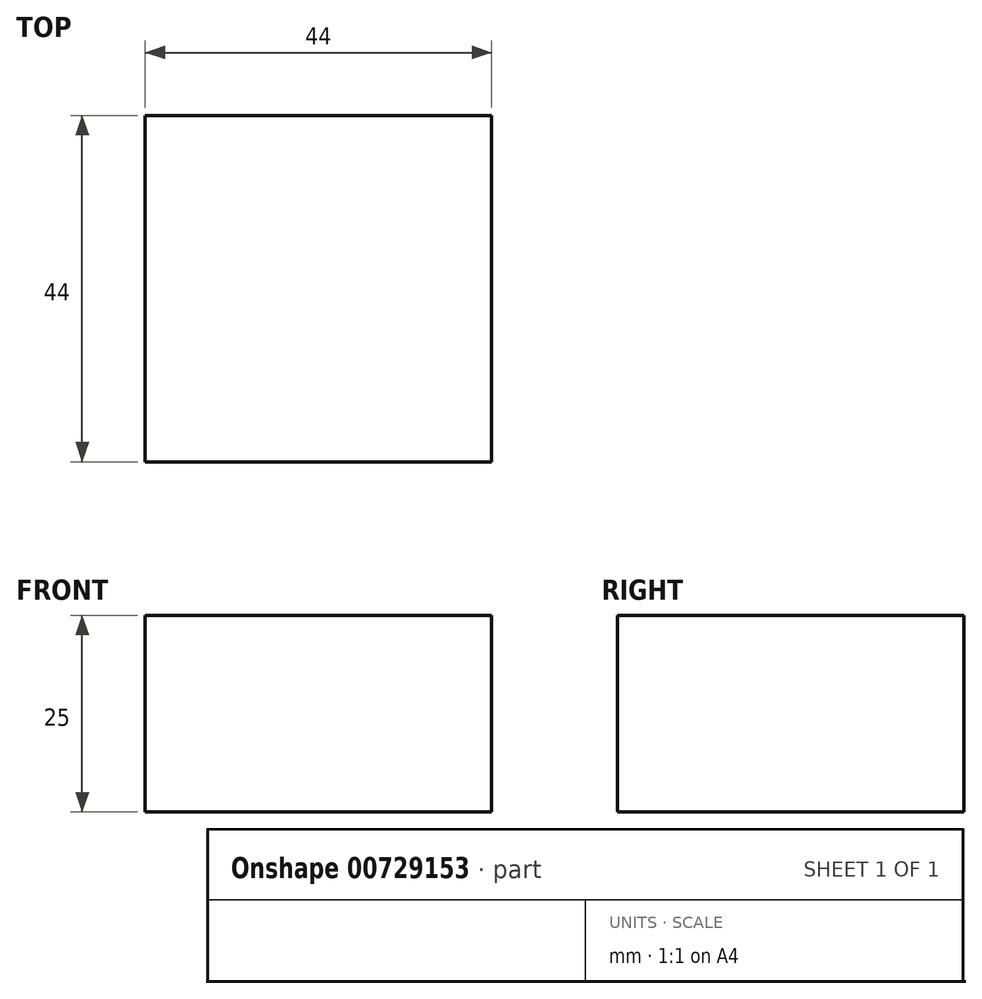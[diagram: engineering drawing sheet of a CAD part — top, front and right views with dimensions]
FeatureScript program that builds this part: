
annotation { "Feature Type Name" : "Feature", "Feature Type Description" : "" }
export const myFeature = defineFeature(function(context is Context, id is Id, definition is map)
    precondition{}
    {
        {
            var Q0;
            Q0=qCreatedBy(makeId("Top.planeOp"),FACE);
            var sketch = newSketch(context, id + "F0", { "sketchPlane" : qUnion([Q0])});
            skLineSegment(sketch, "E0.bottom", {"start": v(22, -22) * mm, "end": v(-22, -22) * mm});
            skLineSegment(sketch, "E0.top", {"start": v(22, 22) * mm, "end": v(-22, 22) * mm});
            skLineSegment(sketch, "E0.left", {"start": v(22, -22) * mm, "end": v(22, 22) * mm});
            skLineSegment(sketch, "E0.right", {"start": v(-22, -22) * mm, "end": v(-22, 22) * mm});
            skPoint(sketch, "E0.middle", {"position": v(0, 0) * mm});
            skSolve(sketch);
        }
        {
            var Q0;
            Q0=makeQuery(id+"F0.imprint","IMPRINT",FACE,{"disambiguationData":[TD([[makeQuery(id+"F0.imprint","IMPRINT",EDGE,{"derivedFrom":sQuery(id+"F0.wireOp",EDGE,"E0.bottom")}),-1.0]])]});
            extrude(context, id + "F1", {"entities" : qUnion([Q0]), "depth" : 25 * mm, "offsetDistance" : 25 * mm});
        }
    });
